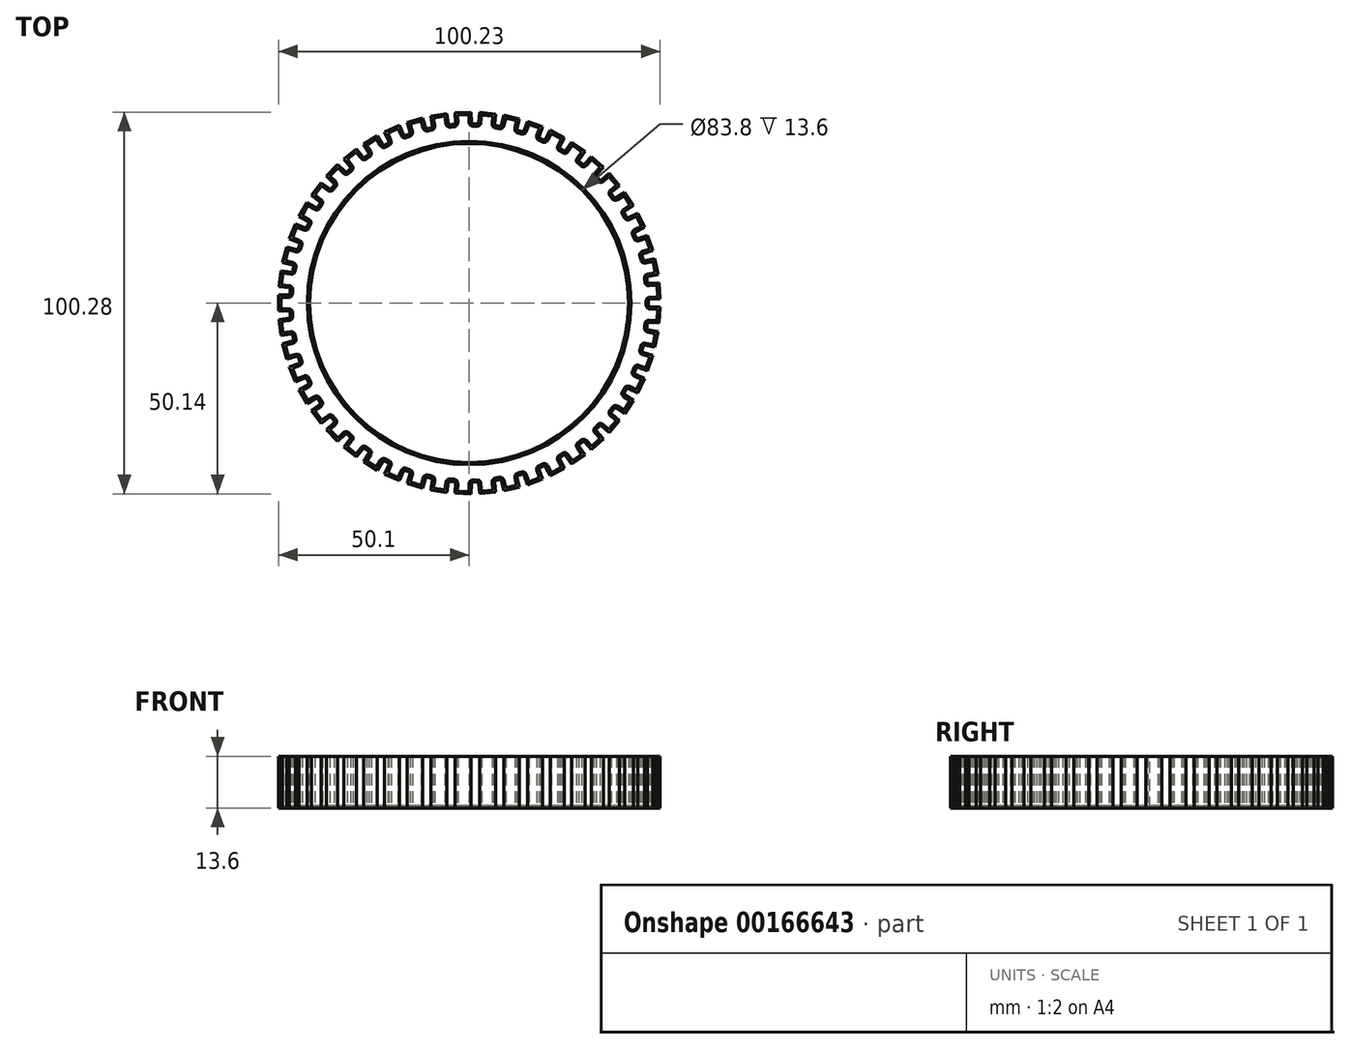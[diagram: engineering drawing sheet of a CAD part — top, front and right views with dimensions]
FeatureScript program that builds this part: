
annotation { "Feature Type Name" : "Feature", "Feature Type Description" : "" }
export const myFeature = defineFeature(function(context is Context, id is Id, definition is map)
    precondition{}
    {
        {
            var Q0;
            Q0=qCreatedBy(makeId("Top.planeOp"),FACE);
            var sketch = newSketch(context, id + "F0", { "sketchPlane" : qUnion([Q0])});
            skCircle(sketch, "E0", {"center": v(0, 0) * mm, "radius": 42.5 * mm});
            skLineSegment(sketch, "E1", {"start": v(0, 0) * mm, "end": v(-65.95, 0) * mm, "construction": true});
            skLineSegment(sketch, "E2.bottom", {"start": v(-49.5, 1.5) * mm, "end": v(-47.43, 1.5) * mm});
            skLineSegment(sketch, "E2.top", {"start": v(-49.5, -1.5) * mm, "end": v(-47.43, -1.5) * mm});
            skLineSegment(sketch, "E2.left", {"start": v(-49.5, 1.5) * mm, "end": v(-49.5, -1.5) * mm});
            skLineSegment(sketch, "E2.right", {"start": v(-43.5, 1.5) * mm, "end": v(-43.5, -1.5) * mm});
            skPoint(sketch, "E2.middle", {"position": v(-46.5, 0) * mm});
            skArc(sketch, "E3", {"start": v(-46.48, 1.5) * mm, "mid": v(-46.5, 0) * mm, "end": v(-46.48, -1.5) * mm});
            skArc(sketch, "E4", {"start": v(-46.44, -2.45) * mm, "mid": v(46.5, 0) * mm, "end": v(-46.44, 2.45) * mm});
            skPoint(sketch, "E5.newPointA", {"position": v(-43.5, 1.5) * mm});
            skArc(sketch, "E5.filletArc", {"start": v(-47.43, 1.5) * mm, "mid": v(-46.75, 1.77) * mm, "end": v(-46.44, 2.45) * mm});
            skPoint(sketch, "E6.newPointB", {"position": v(-43.5, -1.5) * mm});
            skArc(sketch, "E6.filletArc", {"start": v(-46.44, -2.45) * mm, "mid": v(-46.75, -1.77) * mm, "end": v(-47.43, -1.5) * mm});
            skLineSegment(sketch, "E7.1.0", {"start": v(-48.9, 7.82) * mm, "end": v(-46.85, 7.55) * mm});
            skArc(sketch, "E7.1.1", {"start": v(-46.85, 7.55) * mm, "mid": v(-46.14, 7.74) * mm, "end": v(-45.74, 8.37) * mm});
            skLineSegment(sketch, "E7.1.2", {"start": v(-48.9, 7.82) * mm, "end": v(-49.29, 4.84) * mm});
            skLineSegment(sketch, "E7.1.3", {"start": v(-49.29, 4.84) * mm, "end": v(-47.24, 4.58) * mm});
            skArc(sketch, "E7.1.4", {"start": v(-46.37, 3.51) * mm, "mid": v(-46.59, 4.22) * mm, "end": v(-47.24, 4.58) * mm});
            skLineSegment(sketch, "E7.2.0", {"start": v(-47.5, 14) * mm, "end": v(-45.5, 13.48) * mm});
            skArc(sketch, "E7.2.1", {"start": v(-45.5, 13.48) * mm, "mid": v(-44.77, 13.57) * mm, "end": v(-44.3, 14.15) * mm});
            skLineSegment(sketch, "E7.2.2", {"start": v(-47.5, 14) * mm, "end": v(-48.26, 11.1) * mm});
            skLineSegment(sketch, "E7.2.3", {"start": v(-48.26, 11.1) * mm, "end": v(-46.26, 10.58) * mm});
            skArc(sketch, "E7.2.4", {"start": v(-45.54, 9.41) * mm, "mid": v(-45.67, 10.14) * mm, "end": v(-46.26, 10.58) * mm});
            skLineSegment(sketch, "E7.3.0", {"start": v(-45.32, 19.97) * mm, "end": v(-43.4, 19.2) * mm});
            skArc(sketch, "E7.3.1", {"start": v(-43.4, 19.2) * mm, "mid": v(-42.66, 19.19) * mm, "end": v(-42.12, 19.7) * mm});
            skLineSegment(sketch, "E7.3.2", {"start": v(-45.32, 19.97) * mm, "end": v(-46.45, 17.19) * mm});
            skLineSegment(sketch, "E7.3.3", {"start": v(-46.45, 17.19) * mm, "end": v(-44.53, 16.41) * mm});
            skArc(sketch, "E7.3.4", {"start": v(-43.96, 15.16) * mm, "mid": v(-44, 15.9) * mm, "end": v(-44.53, 16.41) * mm});
            skLineSegment(sketch, "E7.4.0", {"start": v(-42.4, 25.6) * mm, "end": v(-40.6, 24.58) * mm});
            skArc(sketch, "E7.4.1", {"start": v(-40.6, 24.58) * mm, "mid": v(-39.86, 24.49) * mm, "end": v(-39.26, 24.92) * mm});
            skLineSegment(sketch, "E7.4.2", {"start": v(-42.4, 25.6) * mm, "end": v(-43.87, 22.98) * mm});
            skLineSegment(sketch, "E7.4.3", {"start": v(-43.87, 22.98) * mm, "end": v(-42.07, 21.97) * mm});
            skArc(sketch, "E7.4.4", {"start": v(-41.66, 20.65) * mm, "mid": v(-41.6, 21.4) * mm, "end": v(-42.07, 21.97) * mm});
            skLineSegment(sketch, "E7.5.0", {"start": v(-38.77, 30.8) * mm, "end": v(-37.12, 29.57) * mm});
            skArc(sketch, "E7.5.1", {"start": v(-37.12, 29.57) * mm, "mid": v(-36.4, 29.38) * mm, "end": v(-35.75, 29.73) * mm});
            skLineSegment(sketch, "E7.5.2", {"start": v(-38.77, 30.8) * mm, "end": v(-40.57, 28.4) * mm});
            skLineSegment(sketch, "E7.5.3", {"start": v(-40.57, 28.4) * mm, "end": v(-38.91, 27.17) * mm});
            skArc(sketch, "E7.5.4", {"start": v(-38.68, 25.81) * mm, "mid": v(-38.52, 26.54) * mm, "end": v(-38.91, 27.17) * mm});
            skLineSegment(sketch, "E7.6.0", {"start": v(-34.51, 35.51) * mm, "end": v(-33.03, 34.08) * mm});
            skArc(sketch, "E7.6.1", {"start": v(-33.03, 34.08) * mm, "mid": v(-32.35, 33.8) * mm, "end": v(-31.65, 34.06) * mm});
            skLineSegment(sketch, "E7.6.2", {"start": v(-34.51, 35.51) * mm, "end": v(-36.6, 33.36) * mm});
            skLineSegment(sketch, "E7.6.3", {"start": v(-36.6, 33.36) * mm, "end": v(-35.12, 31.92) * mm});
            skArc(sketch, "E7.6.4", {"start": v(-35.06, 30.55) * mm, "mid": v(-34.81, 31.25) * mm, "end": v(-35.12, 31.92) * mm});
            skLineSegment(sketch, "E7.7.0", {"start": v(-29.69, 39.64) * mm, "end": v(-28.4, 38.02) * mm});
            skArc(sketch, "E7.7.1", {"start": v(-28.4, 38.02) * mm, "mid": v(-27.76, 37.65) * mm, "end": v(-27.04, 37.83) * mm});
            skLineSegment(sketch, "E7.7.2", {"start": v(-29.69, 39.64) * mm, "end": v(-32.04, 37.77) * mm});
            skLineSegment(sketch, "E7.7.3", {"start": v(-32.04, 37.77) * mm, "end": v(-30.75, 36.15) * mm});
            skArc(sketch, "E7.7.4", {"start": v(-30.87, 34.78) * mm, "mid": v(-30.53, 35.44) * mm, "end": v(-30.75, 36.15) * mm});
            skLineSegment(sketch, "E7.8.0", {"start": v(-24.38, 43.1) * mm, "end": v(-23.3, 41.34) * mm});
            skArc(sketch, "E7.8.1", {"start": v(-23.3, 41.34) * mm, "mid": v(-22.72, 40.9) * mm, "end": v(-21.98, 40.98) * mm});
            skLineSegment(sketch, "E7.8.2", {"start": v(-24.38, 43.1) * mm, "end": v(-26.94, 41.55) * mm});
            skLineSegment(sketch, "E7.8.3", {"start": v(-26.94, 41.55) * mm, "end": v(-25.87, 39.79) * mm});
            skArc(sketch, "E7.8.4", {"start": v(-26.16, 38.44) * mm, "mid": v(-25.75, 39.05) * mm, "end": v(-25.87, 39.79) * mm});
            skLineSegment(sketch, "E7.9.0", {"start": v(-18.67, 45.87) * mm, "end": v(-17.83, 43.98) * mm});
            skArc(sketch, "E7.9.1", {"start": v(-17.83, 43.98) * mm, "mid": v(-17.3, 43.46) * mm, "end": v(-16.56, 43.45) * mm});
            skLineSegment(sketch, "E7.9.2", {"start": v(-18.67, 45.87) * mm, "end": v(-21.4, 44.66) * mm});
            skLineSegment(sketch, "E7.9.3", {"start": v(-21.4, 44.66) * mm, "end": v(-20.57, 42.77) * mm});
            skArc(sketch, "E7.9.4", {"start": v(-21.03, 41.47) * mm, "mid": v(-20.54, 42.03) * mm, "end": v(-20.57, 42.77) * mm});
            skLineSegment(sketch, "E7.10.0", {"start": v(-12.65, 47.88) * mm, "end": v(-12.06, 45.9) * mm});
            skArc(sketch, "E7.10.1", {"start": v(-12.06, 45.9) * mm, "mid": v(-11.6, 45.32) * mm, "end": v(-10.87, 45.21) * mm});
            skLineSegment(sketch, "E7.10.2", {"start": v(-12.65, 47.88) * mm, "end": v(-15.52, 47.03) * mm});
            skLineSegment(sketch, "E7.10.3", {"start": v(-15.52, 47.03) * mm, "end": v(-14.93, 45.05) * mm});
            skArc(sketch, "E7.10.4", {"start": v(-15.56, 43.82) * mm, "mid": v(-15, 44.3) * mm, "end": v(-14.93, 45.05) * mm});
            skLineSegment(sketch, "E7.11.0", {"start": v(-6.42, 49.1) * mm, "end": v(-6.09, 47.07) * mm});
            skArc(sketch, "E7.11.1", {"start": v(-6.09, 47.07) * mm, "mid": v(-5.7, 46.43) * mm, "end": v(-5, 46.23) * mm});
            skLineSegment(sketch, "E7.11.2", {"start": v(-6.42, 49.1) * mm, "end": v(-9.38, 48.63) * mm});
            skLineSegment(sketch, "E7.11.3", {"start": v(-9.38, 48.63) * mm, "end": v(-9.05, 46.59) * mm});
            skArc(sketch, "E7.11.4", {"start": v(-9.83, 45.45) * mm, "mid": v(-9.21, 45.86) * mm, "end": v(-9.05, 46.59) * mm});
            skLineSegment(sketch, "E7.12.0", {"start": v(-0.09, 49.52) * mm, "end": v(-0.02, 47.46) * mm});
            skArc(sketch, "E7.12.1", {"start": v(-0.02, 47.46) * mm, "mid": v(0.28, 46.78) * mm, "end": v(0.96, 46.5) * mm});
            skLineSegment(sketch, "E7.12.2", {"start": v(-0.09, 49.52) * mm, "end": v(-3.09, 49.43) * mm});
            skLineSegment(sketch, "E7.12.3", {"start": v(-3.09, 49.43) * mm, "end": v(-3.02, 47.36) * mm});
            skArc(sketch, "E7.12.4", {"start": v(-3.93, 46.33) * mm, "mid": v(-3.27, 46.67) * mm, "end": v(-3.02, 47.36) * mm});
            skLineSegment(sketch, "E7.13.0", {"start": v(6.25, 49.13) * mm, "end": v(6.05, 47.07) * mm});
            skArc(sketch, "E7.13.1", {"start": v(6.05, 47.07) * mm, "mid": v(6.26, 46.36) * mm, "end": v(6.9, 45.99) * mm});
            skLineSegment(sketch, "E7.13.2", {"start": v(6.25, 49.13) * mm, "end": v(3.26, 49.42) * mm});
            skLineSegment(sketch, "E7.13.3", {"start": v(3.26, 49.42) * mm, "end": v(3.06, 47.36) * mm});
            skArc(sketch, "E7.13.4", {"start": v(2.02, 46.46) * mm, "mid": v(2.72, 46.7) * mm, "end": v(3.06, 47.36) * mm});
            skLineSegment(sketch, "E7.14.0", {"start": v(12.48, 47.93) * mm, "end": v(12.02, 45.91) * mm});
            skArc(sketch, "E7.14.1", {"start": v(12.02, 45.91) * mm, "mid": v(12.13, 45.18) * mm, "end": v(12.72, 44.73) * mm});
            skLineSegment(sketch, "E7.14.2", {"start": v(12.48, 47.93) * mm, "end": v(9.55, 48.6) * mm});
            skLineSegment(sketch, "E7.14.3", {"start": v(9.55, 48.6) * mm, "end": v(9.1, 46.58) * mm});
            skArc(sketch, "E7.14.4", {"start": v(7.95, 45.82) * mm, "mid": v(8.67, 45.97) * mm, "end": v(9.1, 46.58) * mm});
            skLineSegment(sketch, "E7.15.0", {"start": v(18.5, 45.94) * mm, "end": v(17.79, 44) * mm});
            skArc(sketch, "E7.15.1", {"start": v(17.79, 44) * mm, "mid": v(17.8, 43.26) * mm, "end": v(18.33, 42.73) * mm});
            skLineSegment(sketch, "E7.15.2", {"start": v(18.5, 45.94) * mm, "end": v(15.69, 46.97) * mm});
            skLineSegment(sketch, "E7.15.3", {"start": v(15.69, 46.97) * mm, "end": v(14.97, 45.03) * mm});
            skArc(sketch, "E7.15.4", {"start": v(13.74, 44.42) * mm, "mid": v(14.48, 44.48) * mm, "end": v(14.97, 45.03) * mm});
            skLineSegment(sketch, "E7.16.0", {"start": v(24.23, 43.2) * mm, "end": v(23.27, 41.36) * mm});
            skArc(sketch, "E7.16.1", {"start": v(23.27, 41.36) * mm, "mid": v(23.2, 40.62) * mm, "end": v(23.65, 40.04) * mm});
            skLineSegment(sketch, "E7.16.2", {"start": v(24.23, 43.2) * mm, "end": v(21.57, 44.58) * mm});
            skLineSegment(sketch, "E7.16.3", {"start": v(21.57, 44.58) * mm, "end": v(20.61, 42.75) * mm});
            skArc(sketch, "E7.16.4", {"start": v(19.3, 42.3) * mm, "mid": v(20.05, 42.27) * mm, "end": v(20.61, 42.75) * mm});
            skLineSegment(sketch, "E7.17.0", {"start": v(29.55, 39.74) * mm, "end": v(28.37, 38.05) * mm});
            skArc(sketch, "E7.17.1", {"start": v(28.37, 38.05) * mm, "mid": v(28.2, 37.32) * mm, "end": v(28.57, 36.68) * mm});
            skLineSegment(sketch, "E7.17.2", {"start": v(29.55, 39.74) * mm, "end": v(27.09, 41.46) * mm});
            skLineSegment(sketch, "E7.17.3", {"start": v(27.09, 41.46) * mm, "end": v(25.9, 39.76) * mm});
            skArc(sketch, "E7.17.4", {"start": v(24.56, 39.49) * mm, "mid": v(25.29, 39.35) * mm, "end": v(25.9, 39.76) * mm});
            skLineSegment(sketch, "E7.18.0", {"start": v(34.39, 35.64) * mm, "end": v(33, 34.1) * mm});
            skArc(sketch, "E7.18.1", {"start": v(33, 34.1) * mm, "mid": v(32.74, 33.41) * mm, "end": v(33.03, 32.73) * mm});
            skLineSegment(sketch, "E7.18.2", {"start": v(34.39, 35.64) * mm, "end": v(32.17, 37.65) * mm});
            skLineSegment(sketch, "E7.18.3", {"start": v(32.17, 37.65) * mm, "end": v(30.78, 36.12) * mm});
            skArc(sketch, "E7.18.4", {"start": v(29.4, 36.02) * mm, "mid": v(30.11, 35.8) * mm, "end": v(30.78, 36.12) * mm});
            skLineSegment(sketch, "E7.19.0", {"start": v(38.66, 30.95) * mm, "end": v(37.1, 29.6) * mm});
            skArc(sketch, "E7.19.1", {"start": v(37.1, 29.6) * mm, "mid": v(36.74, 28.95) * mm, "end": v(36.94, 28.24) * mm});
            skLineSegment(sketch, "E7.19.2", {"start": v(38.66, 30.95) * mm, "end": v(36.72, 33.23) * mm});
            skLineSegment(sketch, "E7.19.3", {"start": v(36.72, 33.23) * mm, "end": v(35.15, 31.9) * mm});
            skArc(sketch, "E7.19.4", {"start": v(33.77, 31.96) * mm, "mid": v(34.44, 31.65) * mm, "end": v(35.15, 31.9) * mm});
            skLineSegment(sketch, "E7.20.0", {"start": v(42.3, 25.75) * mm, "end": v(40.57, 24.62) * mm});
            skArc(sketch, "E7.20.1", {"start": v(40.57, 24.62) * mm, "mid": v(40.15, 24.01) * mm, "end": v(40.25, 23.28) * mm});
            skLineSegment(sketch, "E7.20.2", {"start": v(42.3, 25.75) * mm, "end": v(40.67, 28.26) * mm});
            skLineSegment(sketch, "E7.20.3", {"start": v(40.67, 28.26) * mm, "end": v(38.94, 27.13) * mm});
            skArc(sketch, "E7.20.4", {"start": v(37.58, 27.38) * mm, "mid": v(38.2, 26.99) * mm, "end": v(38.94, 27.13) * mm});
            skLineSegment(sketch, "E7.21.0", {"start": v(45.25, 20.13) * mm, "end": v(43.39, 19.23) * mm});
            skArc(sketch, "E7.21.1", {"start": v(43.39, 19.23) * mm, "mid": v(42.89, 18.68) * mm, "end": v(42.9, 17.94) * mm});
            skLineSegment(sketch, "E7.21.2", {"start": v(45.25, 20.13) * mm, "end": v(43.95, 22.83) * mm});
            skLineSegment(sketch, "E7.21.3", {"start": v(43.95, 22.83) * mm, "end": v(42.09, 21.93) * mm});
            skArc(sketch, "E7.21.4", {"start": v(40.78, 22.35) * mm, "mid": v(41.35, 21.88) * mm, "end": v(42.09, 21.93) * mm});
            skLineSegment(sketch, "E7.22.0", {"start": v(47.45, 14.17) * mm, "end": v(45.5, 13.52) * mm});
            skArc(sketch, "E7.22.1", {"start": v(45.5, 13.52) * mm, "mid": v(44.92, 13.05) * mm, "end": v(44.84, 12.3) * mm});
            skLineSegment(sketch, "E7.22.2", {"start": v(47.45, 14.17) * mm, "end": v(46.5, 17.02) * mm});
            skLineSegment(sketch, "E7.22.3", {"start": v(46.5, 17.02) * mm, "end": v(44.55, 16.37) * mm});
            skArc(sketch, "E7.22.4", {"start": v(43.3, 16.95) * mm, "mid": v(43.8, 16.41) * mm, "end": v(44.55, 16.37) * mm});
            skLineSegment(sketch, "E7.23.0", {"start": v(48.87, 8) * mm, "end": v(46.85, 7.6) * mm});
            skArc(sketch, "E7.23.1", {"start": v(46.85, 7.6) * mm, "mid": v(46.22, 7.2) * mm, "end": v(46.05, 6.47) * mm});
            skLineSegment(sketch, "E7.23.2", {"start": v(48.87, 8) * mm, "end": v(48.3, 10.93) * mm});
            skLineSegment(sketch, "E7.23.3", {"start": v(48.3, 10.93) * mm, "end": v(46.27, 10.54) * mm});
            skArc(sketch, "E7.23.4", {"start": v(45.11, 11.28) * mm, "mid": v(45.54, 10.68) * mm, "end": v(46.27, 10.54) * mm});
            skLineSegment(sketch, "E7.24.0", {"start": v(49.5, 1.67) * mm, "end": v(47.43, 1.54) * mm});
            skArc(sketch, "E7.24.1", {"start": v(47.43, 1.54) * mm, "mid": v(46.76, 1.22) * mm, "end": v(46.5, 0.53) * mm});
            skLineSegment(sketch, "E7.24.2", {"start": v(49.5, 1.67) * mm, "end": v(49.3, 4.67) * mm});
            skLineSegment(sketch, "E7.24.3", {"start": v(49.3, 4.67) * mm, "end": v(47.24, 4.54) * mm});
            skArc(sketch, "E7.24.4", {"start": v(46.18, 5.42) * mm, "mid": v(46.54, 4.77) * mm, "end": v(47.24, 4.54) * mm});
            skLineSegment(sketch, "E7.25.0", {"start": v(49.3, -4.67) * mm, "end": v(47.24, -4.54) * mm});
            skArc(sketch, "E7.25.1", {"start": v(47.24, -4.54) * mm, "mid": v(46.54, -4.77) * mm, "end": v(46.18, -5.42) * mm});
            skLineSegment(sketch, "E7.25.2", {"start": v(49.3, -4.67) * mm, "end": v(49.5, -1.67) * mm});
            skLineSegment(sketch, "E7.25.3", {"start": v(49.5, -1.67) * mm, "end": v(47.43, -1.54) * mm});
            skArc(sketch, "E7.25.4", {"start": v(46.5, -0.53) * mm, "mid": v(46.76, -1.22) * mm, "end": v(47.43, -1.54) * mm});
            skLineSegment(sketch, "E7.26.0", {"start": v(48.3, -10.93) * mm, "end": v(46.27, -10.54) * mm});
            skArc(sketch, "E7.26.1", {"start": v(46.27, -10.54) * mm, "mid": v(45.54, -10.68) * mm, "end": v(45.11, -11.28) * mm});
            skLineSegment(sketch, "E7.26.2", {"start": v(48.3, -10.93) * mm, "end": v(48.87, -8) * mm});
            skLineSegment(sketch, "E7.26.3", {"start": v(48.87, -8) * mm, "end": v(46.85, -7.6) * mm});
            skArc(sketch, "E7.26.4", {"start": v(46.05, -6.47) * mm, "mid": v(46.22, -7.2) * mm, "end": v(46.85, -7.6) * mm});
            skLineSegment(sketch, "E7.27.0", {"start": v(46.5, -17.02) * mm, "end": v(44.55, -16.37) * mm});
            skArc(sketch, "E7.27.1", {"start": v(44.55, -16.37) * mm, "mid": v(43.8, -16.41) * mm, "end": v(43.3, -16.95) * mm});
            skLineSegment(sketch, "E7.27.2", {"start": v(46.5, -17.02) * mm, "end": v(47.45, -14.17) * mm});
            skLineSegment(sketch, "E7.27.3", {"start": v(47.45, -14.17) * mm, "end": v(45.5, -13.52) * mm});
            skArc(sketch, "E7.27.4", {"start": v(44.84, -12.3) * mm, "mid": v(44.92, -13.05) * mm, "end": v(45.5, -13.52) * mm});
            skLineSegment(sketch, "E7.28.0", {"start": v(43.95, -22.83) * mm, "end": v(42.09, -21.93) * mm});
            skArc(sketch, "E7.28.1", {"start": v(42.09, -21.93) * mm, "mid": v(41.35, -21.88) * mm, "end": v(40.78, -22.35) * mm});
            skLineSegment(sketch, "E7.28.2", {"start": v(43.95, -22.83) * mm, "end": v(45.25, -20.13) * mm});
            skLineSegment(sketch, "E7.28.3", {"start": v(45.25, -20.13) * mm, "end": v(43.39, -19.23) * mm});
            skArc(sketch, "E7.28.4", {"start": v(42.9, -17.94) * mm, "mid": v(42.89, -18.68) * mm, "end": v(43.39, -19.23) * mm});
            skLineSegment(sketch, "E7.29.0", {"start": v(40.67, -28.26) * mm, "end": v(38.94, -27.13) * mm});
            skArc(sketch, "E7.29.1", {"start": v(38.94, -27.13) * mm, "mid": v(38.2, -26.99) * mm, "end": v(37.58, -27.38) * mm});
            skLineSegment(sketch, "E7.29.2", {"start": v(40.67, -28.26) * mm, "end": v(42.3, -25.75) * mm});
            skLineSegment(sketch, "E7.29.3", {"start": v(42.3, -25.75) * mm, "end": v(40.57, -24.62) * mm});
            skArc(sketch, "E7.29.4", {"start": v(40.25, -23.28) * mm, "mid": v(40.15, -24.01) * mm, "end": v(40.57, -24.62) * mm});
            skLineSegment(sketch, "E7.30.0", {"start": v(36.72, -33.23) * mm, "end": v(35.15, -31.9) * mm});
            skArc(sketch, "E7.30.1", {"start": v(35.15, -31.9) * mm, "mid": v(34.44, -31.65) * mm, "end": v(33.77, -31.96) * mm});
            skLineSegment(sketch, "E7.30.2", {"start": v(36.72, -33.23) * mm, "end": v(38.66, -30.95) * mm});
            skLineSegment(sketch, "E7.30.3", {"start": v(38.66, -30.95) * mm, "end": v(37.1, -29.6) * mm});
            skArc(sketch, "E7.30.4", {"start": v(36.94, -28.24) * mm, "mid": v(36.74, -28.95) * mm, "end": v(37.1, -29.6) * mm});
            skLineSegment(sketch, "E7.31.0", {"start": v(32.17, -37.65) * mm, "end": v(30.78, -36.12) * mm});
            skArc(sketch, "E7.31.1", {"start": v(30.78, -36.12) * mm, "mid": v(30.11, -35.8) * mm, "end": v(29.4, -36.02) * mm});
            skLineSegment(sketch, "E7.31.2", {"start": v(32.17, -37.65) * mm, "end": v(34.39, -35.64) * mm});
            skLineSegment(sketch, "E7.31.3", {"start": v(34.39, -35.64) * mm, "end": v(33, -34.1) * mm});
            skArc(sketch, "E7.31.4", {"start": v(33.03, -32.73) * mm, "mid": v(32.74, -33.41) * mm, "end": v(33, -34.1) * mm});
            skLineSegment(sketch, "E7.32.0", {"start": v(27.09, -41.46) * mm, "end": v(25.9, -39.76) * mm});
            skArc(sketch, "E7.32.1", {"start": v(25.9, -39.76) * mm, "mid": v(25.29, -39.35) * mm, "end": v(24.56, -39.49) * mm});
            skLineSegment(sketch, "E7.32.2", {"start": v(27.09, -41.46) * mm, "end": v(29.55, -39.74) * mm});
            skLineSegment(sketch, "E7.32.3", {"start": v(29.55, -39.74) * mm, "end": v(28.37, -38.05) * mm});
            skArc(sketch, "E7.32.4", {"start": v(28.57, -36.68) * mm, "mid": v(28.2, -37.32) * mm, "end": v(28.37, -38.05) * mm});
            skLineSegment(sketch, "E7.33.0", {"start": v(21.57, -44.58) * mm, "end": v(20.61, -42.75) * mm});
            skArc(sketch, "E7.33.1", {"start": v(20.61, -42.75) * mm, "mid": v(20.05, -42.27) * mm, "end": v(19.3, -42.3) * mm});
            skLineSegment(sketch, "E7.33.2", {"start": v(21.57, -44.58) * mm, "end": v(24.23, -43.2) * mm});
            skLineSegment(sketch, "E7.33.3", {"start": v(24.23, -43.2) * mm, "end": v(23.27, -41.36) * mm});
            skArc(sketch, "E7.33.4", {"start": v(23.65, -40.04) * mm, "mid": v(23.2, -40.62) * mm, "end": v(23.27, -41.36) * mm});
            skLineSegment(sketch, "E7.34.0", {"start": v(15.69, -46.97) * mm, "end": v(14.97, -45.03) * mm});
            skArc(sketch, "E7.34.1", {"start": v(14.97, -45.03) * mm, "mid": v(14.48, -44.48) * mm, "end": v(13.74, -44.42) * mm});
            skLineSegment(sketch, "E7.34.2", {"start": v(15.69, -46.97) * mm, "end": v(18.5, -45.94) * mm});
            skLineSegment(sketch, "E7.34.3", {"start": v(18.5, -45.94) * mm, "end": v(17.79, -44) * mm});
            skArc(sketch, "E7.34.4", {"start": v(18.33, -42.73) * mm, "mid": v(17.8, -43.26) * mm, "end": v(17.79, -44) * mm});
            skLineSegment(sketch, "E7.35.0", {"start": v(9.55, -48.6) * mm, "end": v(9.1, -46.58) * mm});
            skArc(sketch, "E7.35.1", {"start": v(9.1, -46.58) * mm, "mid": v(8.67, -45.97) * mm, "end": v(7.95, -45.82) * mm});
            skLineSegment(sketch, "E7.35.2", {"start": v(9.55, -48.6) * mm, "end": v(12.48, -47.93) * mm});
            skLineSegment(sketch, "E7.35.3", {"start": v(12.48, -47.93) * mm, "end": v(12.02, -45.91) * mm});
            skArc(sketch, "E7.35.4", {"start": v(12.72, -44.73) * mm, "mid": v(12.13, -45.18) * mm, "end": v(12.02, -45.91) * mm});
            skLineSegment(sketch, "E7.36.0", {"start": v(3.26, -49.42) * mm, "end": v(3.06, -47.36) * mm});
            skArc(sketch, "E7.36.1", {"start": v(3.06, -47.36) * mm, "mid": v(2.72, -46.7) * mm, "end": v(2.02, -46.46) * mm});
            skLineSegment(sketch, "E7.36.2", {"start": v(3.26, -49.42) * mm, "end": v(6.25, -49.13) * mm});
            skLineSegment(sketch, "E7.36.3", {"start": v(6.25, -49.13) * mm, "end": v(6.05, -47.07) * mm});
            skArc(sketch, "E7.36.4", {"start": v(6.9, -45.99) * mm, "mid": v(6.26, -46.36) * mm, "end": v(6.05, -47.07) * mm});
            skLineSegment(sketch, "E7.37.0", {"start": v(-3.09, -49.43) * mm, "end": v(-3.02, -47.36) * mm});
            skArc(sketch, "E7.37.1", {"start": v(-3.02, -47.36) * mm, "mid": v(-3.27, -46.67) * mm, "end": v(-3.93, -46.33) * mm});
            skLineSegment(sketch, "E7.37.2", {"start": v(-3.09, -49.43) * mm, "end": v(-0.09, -49.52) * mm});
            skLineSegment(sketch, "E7.37.3", {"start": v(-0.09, -49.52) * mm, "end": v(-0.02, -47.46) * mm});
            skArc(sketch, "E7.37.4", {"start": v(0.96, -46.5) * mm, "mid": v(0.28, -46.78) * mm, "end": v(-0.02, -47.46) * mm});
            skLineSegment(sketch, "E7.38.0", {"start": v(-9.38, -48.63) * mm, "end": v(-9.05, -46.59) * mm});
            skArc(sketch, "E7.38.1", {"start": v(-9.05, -46.59) * mm, "mid": v(-9.21, -45.86) * mm, "end": v(-9.83, -45.45) * mm});
            skLineSegment(sketch, "E7.38.2", {"start": v(-9.38, -48.63) * mm, "end": v(-6.42, -49.1) * mm});
            skLineSegment(sketch, "E7.38.3", {"start": v(-6.42, -49.1) * mm, "end": v(-6.09, -47.07) * mm});
            skArc(sketch, "E7.38.4", {"start": v(-5, -46.23) * mm, "mid": v(-5.7, -46.43) * mm, "end": v(-6.09, -47.07) * mm});
            skLineSegment(sketch, "E7.39.0", {"start": v(-15.52, -47.03) * mm, "end": v(-14.93, -45.05) * mm});
            skArc(sketch, "E7.39.1", {"start": v(-14.93, -45.05) * mm, "mid": v(-15, -44.3) * mm, "end": v(-15.56, -43.82) * mm});
            skLineSegment(sketch, "E7.39.2", {"start": v(-15.52, -47.03) * mm, "end": v(-12.65, -47.88) * mm});
            skLineSegment(sketch, "E7.39.3", {"start": v(-12.65, -47.88) * mm, "end": v(-12.06, -45.9) * mm});
            skArc(sketch, "E7.39.4", {"start": v(-10.87, -45.21) * mm, "mid": v(-11.6, -45.32) * mm, "end": v(-12.06, -45.9) * mm});
            skLineSegment(sketch, "E7.40.0", {"start": v(-21.4, -44.66) * mm, "end": v(-20.57, -42.77) * mm});
            skArc(sketch, "E7.40.1", {"start": v(-20.57, -42.77) * mm, "mid": v(-20.54, -42.03) * mm, "end": v(-21.03, -41.47) * mm});
            skLineSegment(sketch, "E7.40.2", {"start": v(-21.4, -44.66) * mm, "end": v(-18.67, -45.87) * mm});
            skLineSegment(sketch, "E7.40.3", {"start": v(-18.67, -45.87) * mm, "end": v(-17.83, -43.98) * mm});
            skArc(sketch, "E7.40.4", {"start": v(-16.56, -43.45) * mm, "mid": v(-17.3, -43.46) * mm, "end": v(-17.83, -43.98) * mm});
            skLineSegment(sketch, "E7.41.0", {"start": v(-26.94, -41.55) * mm, "end": v(-25.87, -39.79) * mm});
            skArc(sketch, "E7.41.1", {"start": v(-25.87, -39.79) * mm, "mid": v(-25.75, -39.05) * mm, "end": v(-26.16, -38.44) * mm});
            skLineSegment(sketch, "E7.41.2", {"start": v(-26.94, -41.55) * mm, "end": v(-24.38, -43.1) * mm});
            skLineSegment(sketch, "E7.41.3", {"start": v(-24.38, -43.1) * mm, "end": v(-23.3, -41.34) * mm});
            skArc(sketch, "E7.41.4", {"start": v(-21.98, -40.98) * mm, "mid": v(-22.72, -40.9) * mm, "end": v(-23.3, -41.34) * mm});
            skLineSegment(sketch, "E7.42.0", {"start": v(-32.04, -37.77) * mm, "end": v(-30.75, -36.15) * mm});
            skArc(sketch, "E7.42.1", {"start": v(-30.75, -36.15) * mm, "mid": v(-30.53, -35.44) * mm, "end": v(-30.87, -34.78) * mm});
            skLineSegment(sketch, "E7.42.2", {"start": v(-32.04, -37.77) * mm, "end": v(-29.69, -39.64) * mm});
            skLineSegment(sketch, "E7.42.3", {"start": v(-29.69, -39.64) * mm, "end": v(-28.4, -38.02) * mm});
            skArc(sketch, "E7.42.4", {"start": v(-27.04, -37.83) * mm, "mid": v(-27.76, -37.65) * mm, "end": v(-28.4, -38.02) * mm});
            skLineSegment(sketch, "E7.43.0", {"start": v(-36.6, -33.36) * mm, "end": v(-35.12, -31.92) * mm});
            skArc(sketch, "E7.43.1", {"start": v(-35.12, -31.92) * mm, "mid": v(-34.81, -31.25) * mm, "end": v(-35.06, -30.55) * mm});
            skLineSegment(sketch, "E7.43.2", {"start": v(-36.6, -33.36) * mm, "end": v(-34.51, -35.51) * mm});
            skLineSegment(sketch, "E7.43.3", {"start": v(-34.51, -35.51) * mm, "end": v(-33.03, -34.08) * mm});
            skArc(sketch, "E7.43.4", {"start": v(-31.65, -34.06) * mm, "mid": v(-32.35, -33.8) * mm, "end": v(-33.03, -34.08) * mm});
            skLineSegment(sketch, "E7.44.0", {"start": v(-40.57, -28.4) * mm, "end": v(-38.91, -27.17) * mm});
            skArc(sketch, "E7.44.1", {"start": v(-38.91, -27.17) * mm, "mid": v(-38.52, -26.54) * mm, "end": v(-38.68, -25.81) * mm});
            skLineSegment(sketch, "E7.44.2", {"start": v(-40.57, -28.4) * mm, "end": v(-38.77, -30.8) * mm});
            skLineSegment(sketch, "E7.44.3", {"start": v(-38.77, -30.8) * mm, "end": v(-37.12, -29.57) * mm});
            skArc(sketch, "E7.44.4", {"start": v(-35.75, -29.73) * mm, "mid": v(-36.4, -29.38) * mm, "end": v(-37.12, -29.57) * mm});
            skLineSegment(sketch, "E7.45.0", {"start": v(-43.87, -22.98) * mm, "end": v(-42.07, -21.97) * mm});
            skArc(sketch, "E7.45.1", {"start": v(-42.07, -21.97) * mm, "mid": v(-41.6, -21.4) * mm, "end": v(-41.66, -20.65) * mm});
            skLineSegment(sketch, "E7.45.2", {"start": v(-43.87, -22.98) * mm, "end": v(-42.4, -25.6) * mm});
            skLineSegment(sketch, "E7.45.3", {"start": v(-42.4, -25.6) * mm, "end": v(-40.6, -24.58) * mm});
            skArc(sketch, "E7.45.4", {"start": v(-39.26, -24.92) * mm, "mid": v(-39.86, -24.49) * mm, "end": v(-40.6, -24.58) * mm});
            skLineSegment(sketch, "E7.46.0", {"start": v(-46.45, -17.19) * mm, "end": v(-44.53, -16.41) * mm});
            skArc(sketch, "E7.46.1", {"start": v(-44.53, -16.41) * mm, "mid": v(-44, -15.9) * mm, "end": v(-43.96, -15.16) * mm});
            skLineSegment(sketch, "E7.46.2", {"start": v(-46.45, -17.19) * mm, "end": v(-45.32, -19.97) * mm});
            skLineSegment(sketch, "E7.46.3", {"start": v(-45.32, -19.97) * mm, "end": v(-43.4, -19.2) * mm});
            skArc(sketch, "E7.46.4", {"start": v(-42.12, -19.7) * mm, "mid": v(-42.66, -19.19) * mm, "end": v(-43.4, -19.2) * mm});
            skLineSegment(sketch, "E7.47.0", {"start": v(-48.26, -11.1) * mm, "end": v(-46.26, -10.58) * mm});
            skArc(sketch, "E7.47.1", {"start": v(-46.26, -10.58) * mm, "mid": v(-45.67, -10.14) * mm, "end": v(-45.54, -9.41) * mm});
            skLineSegment(sketch, "E7.47.2", {"start": v(-48.26, -11.1) * mm, "end": v(-47.5, -14) * mm});
            skLineSegment(sketch, "E7.47.3", {"start": v(-47.5, -14) * mm, "end": v(-45.5, -13.48) * mm});
            skArc(sketch, "E7.47.4", {"start": v(-44.3, -14.15) * mm, "mid": v(-44.77, -13.57) * mm, "end": v(-45.5, -13.48) * mm});
            skLineSegment(sketch, "E7.48.0", {"start": v(-49.29, -4.84) * mm, "end": v(-47.24, -4.58) * mm});
            skArc(sketch, "E7.48.1", {"start": v(-47.24, -4.58) * mm, "mid": v(-46.59, -4.22) * mm, "end": v(-46.37, -3.51) * mm});
            skLineSegment(sketch, "E7.48.2", {"start": v(-49.29, -4.84) * mm, "end": v(-48.9, -7.82) * mm});
            skLineSegment(sketch, "E7.48.3", {"start": v(-48.9, -7.82) * mm, "end": v(-46.85, -7.55) * mm});
            skArc(sketch, "E7.48.4", {"start": v(-45.74, -8.37) * mm, "mid": v(-46.14, -7.74) * mm, "end": v(-46.85, -7.55) * mm});
            skLineSegment(sketch, "E7.anchor1", {"start": v(0, 0) * mm, "end": v(-49.5, -1.5) * mm, "construction": true});
            skLineSegment(sketch, "E7.anchor2", {"start": v(0, 0) * mm, "end": v(-49.5, -1.5) * mm, "construction": true});
            skSolve(sketch);
        }
        {
            var Q0;
            Q0 = qSketchRegion(id + "F0", true);
            extrude(context, id + "F1", {"entities" : qUnion([Q0]), "depth" : 13 * mm});
        }
        {
            var Q0;
            Q0=makeQuery(id+"F1.opExtrude","CAP_FACE",FACE,{"disambiguationData":[OSD([sQuery(id+"F0.wireOp",EDGE,"E0"),sQuery(id+"F0.wireOp",EDGE,"E4"),sQuery(id+"F0.wireOp",EDGE,"E7.1.0"),sQuery(id+"F0.wireOp",EDGE,"E7.1.1"),sQuery(id+"F0.wireOp",EDGE,"E7.1.2"),sQuery(id+"F0.wireOp",EDGE,"E7.1.3"),sQuery(id+"F0.wireOp",EDGE,"E7.1.4"),sQuery(id+"F0.wireOp",EDGE,"E7.2.0"),sQuery(id+"F0.wireOp",EDGE,"E7.2.1"),sQuery(id+"F0.wireOp",EDGE,"E7.2.2"),sQuery(id+"F0.wireOp",EDGE,"E7.2.3"),sQuery(id+"F0.wireOp",EDGE,"E7.2.4"),sQuery(id+"F0.wireOp",EDGE,"E7.3.0"),sQuery(id+"F0.wireOp",EDGE,"E7.3.1"),sQuery(id+"F0.wireOp",EDGE,"E7.3.2"),sQuery(id+"F0.wireOp",EDGE,"E7.3.3"),sQuery(id+"F0.wireOp",EDGE,"E7.3.4"),sQuery(id+"F0.wireOp",EDGE,"E7.4.0"),sQuery(id+"F0.wireOp",EDGE,"E7.4.1"),sQuery(id+"F0.wireOp",EDGE,"E7.4.2"),sQuery(id+"F0.wireOp",EDGE,"E7.4.3"),sQuery(id+"F0.wireOp",EDGE,"E7.4.4"),sQuery(id+"F0.wireOp",EDGE,"E7.5.0"),sQuery(id+"F0.wireOp",EDGE,"E7.5.1"),sQuery(id+"F0.wireOp",EDGE,"E7.5.2"),sQuery(id+"F0.wireOp",EDGE,"E7.5.3"),sQuery(id+"F0.wireOp",EDGE,"E7.5.4"),sQuery(id+"F0.wireOp",EDGE,"E7.6.0"),sQuery(id+"F0.wireOp",EDGE,"E7.6.1"),sQuery(id+"F0.wireOp",EDGE,"E7.6.2"),sQuery(id+"F0.wireOp",EDGE,"E7.6.3"),sQuery(id+"F0.wireOp",EDGE,"E7.6.4"),sQuery(id+"F0.wireOp",EDGE,"E7.7.0"),sQuery(id+"F0.wireOp",EDGE,"E7.7.1"),sQuery(id+"F0.wireOp",EDGE,"E7.7.2"),sQuery(id+"F0.wireOp",EDGE,"E7.7.3"),sQuery(id+"F0.wireOp",EDGE,"E7.7.4"),sQuery(id+"F0.wireOp",EDGE,"E7.8.0"),sQuery(id+"F0.wireOp",EDGE,"E7.8.1"),sQuery(id+"F0.wireOp",EDGE,"E7.8.2"),sQuery(id+"F0.wireOp",EDGE,"E7.8.3"),sQuery(id+"F0.wireOp",EDGE,"E7.8.4"),sQuery(id+"F0.wireOp",EDGE,"E7.9.0"),sQuery(id+"F0.wireOp",EDGE,"E7.9.1"),sQuery(id+"F0.wireOp",EDGE,"E7.9.2"),sQuery(id+"F0.wireOp",EDGE,"E7.9.3"),sQuery(id+"F0.wireOp",EDGE,"E7.9.4"),sQuery(id+"F0.wireOp",EDGE,"E7.10.0"),sQuery(id+"F0.wireOp",EDGE,"E7.10.1"),sQuery(id+"F0.wireOp",EDGE,"E7.10.2"),sQuery(id+"F0.wireOp",EDGE,"E7.10.3"),sQuery(id+"F0.wireOp",EDGE,"E7.10.4"),sQuery(id+"F0.wireOp",EDGE,"E7.11.0"),sQuery(id+"F0.wireOp",EDGE,"E7.11.1"),sQuery(id+"F0.wireOp",EDGE,"E7.11.2"),sQuery(id+"F0.wireOp",EDGE,"E7.11.3"),sQuery(id+"F0.wireOp",EDGE,"E7.11.4"),sQuery(id+"F0.wireOp",EDGE,"E7.12.0"),sQuery(id+"F0.wireOp",EDGE,"E7.12.1"),sQuery(id+"F0.wireOp",EDGE,"E7.12.2"),sQuery(id+"F0.wireOp",EDGE,"E7.12.3"),sQuery(id+"F0.wireOp",EDGE,"E7.12.4"),sQuery(id+"F0.wireOp",EDGE,"E7.13.0"),sQuery(id+"F0.wireOp",EDGE,"E7.13.1"),sQuery(id+"F0.wireOp",EDGE,"E7.13.2"),sQuery(id+"F0.wireOp",EDGE,"E7.13.3"),sQuery(id+"F0.wireOp",EDGE,"E7.13.4"),sQuery(id+"F0.wireOp",EDGE,"E7.14.0"),sQuery(id+"F0.wireOp",EDGE,"E7.14.1"),sQuery(id+"F0.wireOp",EDGE,"E7.14.2"),sQuery(id+"F0.wireOp",EDGE,"E7.14.3"),sQuery(id+"F0.wireOp",EDGE,"E7.14.4"),sQuery(id+"F0.wireOp",EDGE,"E7.15.0"),sQuery(id+"F0.wireOp",EDGE,"E7.15.1"),sQuery(id+"F0.wireOp",EDGE,"E7.15.2"),sQuery(id+"F0.wireOp",EDGE,"E7.15.3"),sQuery(id+"F0.wireOp",EDGE,"E7.15.4"),sQuery(id+"F0.wireOp",EDGE,"E7.16.0"),sQuery(id+"F0.wireOp",EDGE,"E7.16.1"),sQuery(id+"F0.wireOp",EDGE,"E7.16.2"),sQuery(id+"F0.wireOp",EDGE,"E7.16.3"),sQuery(id+"F0.wireOp",EDGE,"E7.16.4"),sQuery(id+"F0.wireOp",EDGE,"E7.17.0"),sQuery(id+"F0.wireOp",EDGE,"E7.17.1"),sQuery(id+"F0.wireOp",EDGE,"E7.17.2"),sQuery(id+"F0.wireOp",EDGE,"E7.17.3"),sQuery(id+"F0.wireOp",EDGE,"E7.17.4"),sQuery(id+"F0.wireOp",EDGE,"E7.18.0"),sQuery(id+"F0.wireOp",EDGE,"E7.18.1"),sQuery(id+"F0.wireOp",EDGE,"E7.18.2"),sQuery(id+"F0.wireOp",EDGE,"E7.18.3"),sQuery(id+"F0.wireOp",EDGE,"E7.18.4"),sQuery(id+"F0.wireOp",EDGE,"E7.19.0"),sQuery(id+"F0.wireOp",EDGE,"E7.19.1"),sQuery(id+"F0.wireOp",EDGE,"E7.19.2"),sQuery(id+"F0.wireOp",EDGE,"E7.19.3"),sQuery(id+"F0.wireOp",EDGE,"E7.19.4"),sQuery(id+"F0.wireOp",EDGE,"E7.20.0"),sQuery(id+"F0.wireOp",EDGE,"E7.20.1"),sQuery(id+"F0.wireOp",EDGE,"E7.20.2"),sQuery(id+"F0.wireOp",EDGE,"E7.20.3"),sQuery(id+"F0.wireOp",EDGE,"E7.20.4"),sQuery(id+"F0.wireOp",EDGE,"E7.21.0"),sQuery(id+"F0.wireOp",EDGE,"E7.21.1"),sQuery(id+"F0.wireOp",EDGE,"E7.21.2"),sQuery(id+"F0.wireOp",EDGE,"E7.21.3"),sQuery(id+"F0.wireOp",EDGE,"E7.21.4"),sQuery(id+"F0.wireOp",EDGE,"E7.22.0"),sQuery(id+"F0.wireOp",EDGE,"E7.22.1"),sQuery(id+"F0.wireOp",EDGE,"E7.22.2"),sQuery(id+"F0.wireOp",EDGE,"E7.22.3"),sQuery(id+"F0.wireOp",EDGE,"E7.22.4"),sQuery(id+"F0.wireOp",EDGE,"E7.23.0"),sQuery(id+"F0.wireOp",EDGE,"E7.23.1"),sQuery(id+"F0.wireOp",EDGE,"E7.23.2"),sQuery(id+"F0.wireOp",EDGE,"E7.23.3"),sQuery(id+"F0.wireOp",EDGE,"E7.23.4"),sQuery(id+"F0.wireOp",EDGE,"E7.24.0"),sQuery(id+"F0.wireOp",EDGE,"E7.24.1"),sQuery(id+"F0.wireOp",EDGE,"E7.24.2"),sQuery(id+"F0.wireOp",EDGE,"E7.24.3"),sQuery(id+"F0.wireOp",EDGE,"E7.24.4"),sQuery(id+"F0.wireOp",EDGE,"E7.25.0"),sQuery(id+"F0.wireOp",EDGE,"E7.25.1"),sQuery(id+"F0.wireOp",EDGE,"E7.25.2"),sQuery(id+"F0.wireOp",EDGE,"E7.25.3"),sQuery(id+"F0.wireOp",EDGE,"E7.25.4"),sQuery(id+"F0.wireOp",EDGE,"E7.26.0"),sQuery(id+"F0.wireOp",EDGE,"E7.26.1"),sQuery(id+"F0.wireOp",EDGE,"E7.26.2"),sQuery(id+"F0.wireOp",EDGE,"E7.26.3"),sQuery(id+"F0.wireOp",EDGE,"E7.26.4"),sQuery(id+"F0.wireOp",EDGE,"E7.27.0"),sQuery(id+"F0.wireOp",EDGE,"E7.27.1"),sQuery(id+"F0.wireOp",EDGE,"E7.27.2"),sQuery(id+"F0.wireOp",EDGE,"E7.27.3"),sQuery(id+"F0.wireOp",EDGE,"E7.27.4"),sQuery(id+"F0.wireOp",EDGE,"E7.28.0"),sQuery(id+"F0.wireOp",EDGE,"E7.28.1"),sQuery(id+"F0.wireOp",EDGE,"E7.28.2"),sQuery(id+"F0.wireOp",EDGE,"E7.28.3"),sQuery(id+"F0.wireOp",EDGE,"E7.28.4"),sQuery(id+"F0.wireOp",EDGE,"E7.29.0"),sQuery(id+"F0.wireOp",EDGE,"E7.29.1"),sQuery(id+"F0.wireOp",EDGE,"E7.29.2"),sQuery(id+"F0.wireOp",EDGE,"E7.29.3"),sQuery(id+"F0.wireOp",EDGE,"E7.29.4"),sQuery(id+"F0.wireOp",EDGE,"E7.30.0"),sQuery(id+"F0.wireOp",EDGE,"E7.30.1"),sQuery(id+"F0.wireOp",EDGE,"E7.30.2"),sQuery(id+"F0.wireOp",EDGE,"E7.30.3"),sQuery(id+"F0.wireOp",EDGE,"E7.30.4"),sQuery(id+"F0.wireOp",EDGE,"E7.31.0"),sQuery(id+"F0.wireOp",EDGE,"E7.31.1"),sQuery(id+"F0.wireOp",EDGE,"E7.31.2"),sQuery(id+"F0.wireOp",EDGE,"E7.31.3"),sQuery(id+"F0.wireOp",EDGE,"E7.31.4"),sQuery(id+"F0.wireOp",EDGE,"E7.32.0"),sQuery(id+"F0.wireOp",EDGE,"E7.32.1"),sQuery(id+"F0.wireOp",EDGE,"E7.32.2"),sQuery(id+"F0.wireOp",EDGE,"E7.32.3"),sQuery(id+"F0.wireOp",EDGE,"E7.32.4"),sQuery(id+"F0.wireOp",EDGE,"E7.33.0"),sQuery(id+"F0.wireOp",EDGE,"E7.33.1"),sQuery(id+"F0.wireOp",EDGE,"E7.33.2"),sQuery(id+"F0.wireOp",EDGE,"E7.33.3"),sQuery(id+"F0.wireOp",EDGE,"E7.33.4"),sQuery(id+"F0.wireOp",EDGE,"E7.34.0"),sQuery(id+"F0.wireOp",EDGE,"E7.34.1"),sQuery(id+"F0.wireOp",EDGE,"E7.34.2"),sQuery(id+"F0.wireOp",EDGE,"E7.34.3"),sQuery(id+"F0.wireOp",EDGE,"E7.34.4"),sQuery(id+"F0.wireOp",EDGE,"E7.35.0"),sQuery(id+"F0.wireOp",EDGE,"E7.35.1"),sQuery(id+"F0.wireOp",EDGE,"E7.35.2"),sQuery(id+"F0.wireOp",EDGE,"E7.35.3"),sQuery(id+"F0.wireOp",EDGE,"E7.35.4"),sQuery(id+"F0.wireOp",EDGE,"E7.36.0"),sQuery(id+"F0.wireOp",EDGE,"E7.36.1"),sQuery(id+"F0.wireOp",EDGE,"E7.36.2"),sQuery(id+"F0.wireOp",EDGE,"E7.36.3"),sQuery(id+"F0.wireOp",EDGE,"E7.36.4"),sQuery(id+"F0.wireOp",EDGE,"E7.37.0"),sQuery(id+"F0.wireOp",EDGE,"E7.37.1"),sQuery(id+"F0.wireOp",EDGE,"E7.37.2"),sQuery(id+"F0.wireOp",EDGE,"E7.37.3"),sQuery(id+"F0.wireOp",EDGE,"E7.37.4"),sQuery(id+"F0.wireOp",EDGE,"E7.38.0"),sQuery(id+"F0.wireOp",EDGE,"E7.38.1"),sQuery(id+"F0.wireOp",EDGE,"E7.38.2"),sQuery(id+"F0.wireOp",EDGE,"E7.38.3"),sQuery(id+"F0.wireOp",EDGE,"E7.38.4"),sQuery(id+"F0.wireOp",EDGE,"E7.39.0"),sQuery(id+"F0.wireOp",EDGE,"E7.39.1"),sQuery(id+"F0.wireOp",EDGE,"E7.39.2"),sQuery(id+"F0.wireOp",EDGE,"E7.39.3"),sQuery(id+"F0.wireOp",EDGE,"E7.39.4"),sQuery(id+"F0.wireOp",EDGE,"E7.40.0"),sQuery(id+"F0.wireOp",EDGE,"E7.40.1"),sQuery(id+"F0.wireOp",EDGE,"E7.40.2"),sQuery(id+"F0.wireOp",EDGE,"E7.40.3"),sQuery(id+"F0.wireOp",EDGE,"E7.40.4"),sQuery(id+"F0.wireOp",EDGE,"E7.41.0"),sQuery(id+"F0.wireOp",EDGE,"E7.41.1"),sQuery(id+"F0.wireOp",EDGE,"E7.41.2"),sQuery(id+"F0.wireOp",EDGE,"E7.41.3"),sQuery(id+"F0.wireOp",EDGE,"E7.41.4"),sQuery(id+"F0.wireOp",EDGE,"E7.42.0"),sQuery(id+"F0.wireOp",EDGE,"E7.42.1"),sQuery(id+"F0.wireOp",EDGE,"E7.42.2"),sQuery(id+"F0.wireOp",EDGE,"E7.42.3"),sQuery(id+"F0.wireOp",EDGE,"E7.42.4"),sQuery(id+"F0.wireOp",EDGE,"E7.43.0"),sQuery(id+"F0.wireOp",EDGE,"E7.43.1"),sQuery(id+"F0.wireOp",EDGE,"E7.43.2"),sQuery(id+"F0.wireOp",EDGE,"E7.43.3"),sQuery(id+"F0.wireOp",EDGE,"E7.43.4"),sQuery(id+"F0.wireOp",EDGE,"E7.44.0"),sQuery(id+"F0.wireOp",EDGE,"E7.44.1"),sQuery(id+"F0.wireOp",EDGE,"E7.44.2"),sQuery(id+"F0.wireOp",EDGE,"E7.44.3"),sQuery(id+"F0.wireOp",EDGE,"E7.44.4"),sQuery(id+"F0.wireOp",EDGE,"E7.45.0"),sQuery(id+"F0.wireOp",EDGE,"E7.45.1"),sQuery(id+"F0.wireOp",EDGE,"E7.45.2"),sQuery(id+"F0.wireOp",EDGE,"E7.45.3"),sQuery(id+"F0.wireOp",EDGE,"E7.45.4"),sQuery(id+"F0.wireOp",EDGE,"E7.46.0"),sQuery(id+"F0.wireOp",EDGE,"E7.46.1"),sQuery(id+"F0.wireOp",EDGE,"E7.46.2"),sQuery(id+"F0.wireOp",EDGE,"E7.46.3"),sQuery(id+"F0.wireOp",EDGE,"E7.46.4"),sQuery(id+"F0.wireOp",EDGE,"E7.47.0"),sQuery(id+"F0.wireOp",EDGE,"E7.47.1"),sQuery(id+"F0.wireOp",EDGE,"E7.47.2"),sQuery(id+"F0.wireOp",EDGE,"E7.47.3"),sQuery(id+"F0.wireOp",EDGE,"E7.47.4"),sQuery(id+"F0.wireOp",EDGE,"E7.48.0"),sQuery(id+"F0.wireOp",EDGE,"E7.48.1"),sQuery(id+"F0.wireOp",EDGE,"E7.48.2"),sQuery(id+"F0.wireOp",EDGE,"E7.48.3"),sQuery(id+"F0.wireOp",EDGE,"E7.48.4"),sQuery(id+"F0.wireOp",EDGE,"E2.bottom"),sQuery(id+"F0.wireOp",EDGE,"E5.filletArc"),sQuery(id+"F0.wireOp",EDGE,"E2.left"),sQuery(id+"F0.wireOp",EDGE,"E2.top"),sQuery(id+"F0.wireOp",EDGE,"E6.filletArc")])],"isStart":false});
            shell(context, id + "F2", {"entities" : qUnion([Q0]), "thickness" : 0.6 * mm, "oppositeDirection" : true});
        }
    });
